FCSTD DOCUMENT  (FreeCAD 1.0R39285 (Git))
Label: GateValve
License: All rights reserved
LicenseURL: https://en.wikipedia.org/wiki/All_rights_reserved
objects: Part::Cylinder×23, Part::MultiFuse×20, Part::Cut×18, Part::Mirroring×12, Part::Box×12, Part::FeaturePython×11, Part::Feature×11, Sketcher::SketchObject×6, PartDesign::Pad×6, PartDesign::Body×6, Part::Torus×6, Part::MultiCommon×3
note: 152 computed .brp shape members not serialized (recipe doc carries the construction recipe); baked Part::Feature solids carry a one-line shape summary decoded from their .brp

FEATURE [Part::FeaturePython] Tube  label="IGP_Bellow"  # WARN: FeaturePython — macro-defined, semantics opaque (R4)
  AttacherType = Attacher::AttachEngine3D
  Height = 47
  InnerRadius = 11
  OuterRadius = 12.5
  Placement = pos=(0,0,114) rot=(0,1,0;0rad)
FEATURE [Part::Feature] Part__Feature1456  label="PrecursorTMP"
  Placement = pos=(0,40,0) rot=(0,1,0;1.5708rad)
  shape: bbox 254 x 24.64 x 254 mm, 51 faces (baked)
FEATURE [Part::Feature] Part__Feature  label="wh"
  Placement = pos=(0,0,0) rot=(1,0,0;1.5708rad)
  shape: bbox 69.9 x 69.9 x 12.7 mm, 278 faces (baked)
FEATURE [Part::FeaturePython] Tube001  # WARN: FeaturePython — macro-defined, semantics opaque (R4)
  AttacherType = Attacher::AttachEngine3D
  Height = 10.5
  InnerRadius = 32
  OuterRadius = 34.95
  Placement = pos=(0,0,1) rot=(0,0,1;0rad)
FEATURE [Part::MultiFuse] Fusion001  label="PreIGP"
  Placement = pos=(0,20,0) rot=(1,0,0;4.71239rad)
  Shapes = -> [Part__Feature,Tube001]
FEATURE [Part::Feature] Part__Feature1457  label="190094"
  shape: bbox 152.3 x 19.8 x 152.3 mm, 298 faces (baked)
FEATURE [Part::FeaturePython] Tube002  # WARN: FeaturePython — macro-defined, semantics opaque (R4)
  AttacherType = Attacher::AttachEngine3D
  Height = 18
  InnerRadius = 74
  OuterRadius = 76.15
  Placement = pos=(0,19,0) rot=(1,0,0;1.5708rad)
FEATURE [Part::MultiFuse] Fusion002  label="BAFlange"
  Placement = pos=(0,25,0) rot=(0,0,1;0rad)
  Shapes = -> [Part__Feature1457,Tube002]
FEATURE [Part::FeaturePython] Tube003  # WARN: FeaturePython — macro-defined, semantics opaque (R4)
  AttacherType = Attacher::AttachEngine3D
  Height = 20
  InnerRadius = 100
  OuterRadius = 110
  Placement = pos=(0,40,0) rot=(1,0,0;1.5708rad)
FEATURE [Part::MultiFuse] Fusion
  Shapes = -> [Part__Feature1456,Tube003]
FEATURE [Part::Mirroring] Part__Mirroring  label="PrecTMP"
  Base = (0,0,0)
  Normal = (0,1,0)
  Source = -> Fusion
FEATURE [Part::Box] Box  label="Cube"
  AttacherType = Attacher::AttachEngine3D
  Height = 500
  Length = 240
  Placement = pos=(-120,-25,-150) rot=(0,0,1;0rad)
  Width = 50
FEATURE [Part::FeaturePython] Tube004  # WARN: FeaturePython — macro-defined, semantics opaque (R4)
  AttacherType = Attacher::AttachEngine3D
  Height = 100
  InnerRadius = 0
  OuterRadius = 100
  Placement = pos=(0,40,0) rot=(1,0,0;1.5708rad)
FEATURE [Part::Cut] Cut
  Base = -> Box
  Tool = -> Tube004
FEATURE [Part::FeaturePython] Tube005  # WARN: FeaturePython — macro-defined, semantics opaque (R4)
  AttacherType = Attacher::AttachEngine3D
  Height = 12
  InnerRadius = 52
  OuterRadius = 58
  Placement = pos=(0,25,0) rot=(1,0,0;1.5708rad)
FEATURE [Part::MultiFuse] Fusion004
  Shapes = -> [Tube005,Fusion002]
FEATURE [Part::Mirroring] Part__Mirroring001  label="Gague"
  Base = (0,0,0)
  Normal = (0,1,0)
  Source = -> Fusion004
FEATURE [Part::Box] Box002  label="Cube002"
  AttacherType = Attacher::AttachEngine3D
  Height = 300
  Length = 140
  Placement = pos=(-70,-17,-90) rot=(0,0,1;0rad)
  Width = 34
FEATURE [Part::FeaturePython] Tube006  # WARN: FeaturePython — macro-defined, semantics opaque (R4)
  AttacherType = Attacher::AttachEngine3D
  Height = 100
  InnerRadius = 0
  OuterRadius = 52
  Placement = pos=(0,50,0) rot=(1,0,0;1.5708rad)
FEATURE [Part::Cut] Cut002
  Base = -> Box002
  Tool = -> Tube006
FEATURE [Part::FeaturePython] Tube007  # WARN: FeaturePython — macro-defined, semantics opaque (R4)
  AttacherType = Attacher::AttachEngine3D
  Height = 8
  InnerRadius = 20
  OuterRadius = 25
  Placement = pos=(0,20,0) rot=(1,0,0;1.5708rad)
FEATURE [Part::MultiFuse] Fusion006
  Shapes = -> [Tube007,Fusion001]
FEATURE [Part::Mirroring] Part__Mirroring002  label="Flangelets"
  Base = (0,0,0)
  Normal = (0,1,0)
  Source = -> Fusion006
FEATURE [Part::Box] Box004  label="Cube004"
  AttacherType = Attacher::AttachEngine3D
  Height = 168
  Length = 60
  Placement = pos=(-30,-14,-58) rot=(0,0,1;0rad)
  Width = 28
FEATURE [Part::FeaturePython] Tube008  # WARN: FeaturePython — macro-defined, semantics opaque (R4)
  AttacherType = Attacher::AttachEngine3D
  Height = 100
  InnerRadius = 0
  OuterRadius = 20
  Placement = pos=(0,50,0) rot=(1,0,0;1.5708rad)
FEATURE [Sketcher::SketchObject] Sketch
  ArcFitTolerance = 1e-06
  AttachmentSupport = -> [YZ_Plane]
  FullyConstrained = true
  MakeInternals = false
  MapMode = 5
  Placement = pos=(0,0,0) rot=(0.57735,0.57735,0.57735;2.0944rad)
  sketch-geometry (4):
    g0: LineSegment StartX=0 StartY=0 StartZ=0 EndX=10 EndY=0 EndZ=0
    g1: LineSegment StartX=0 StartY=0 StartZ=0 EndX=0 EndY=-156 EndZ=0
    g2: LineSegment StartX=0 StartY=-156 StartZ=0 EndX=4 EndY=-156 EndZ=0
    g3: LineSegment StartX=10 StartY=0 StartZ=0 EndX=4 EndY=-156 EndZ=0
  constraints (11):
    c: Distance(g0) = 10
    c: Coincident(g0,g-1)
    c: PointOnObject(g0,g-1)
    c: Distance(g1) = 156
    c: Coincident(g1,g0)
    c: Vertical(g1)
    c: Distance(g2) = 4
    c: Coincident(g2,g1)
    c: Horizontal(g2)
    c: Coincident(g3,g0)
    c: Coincident(g3,g2)
FEATURE [PartDesign::Pad] Pad
  Direction = (1,0,0)
  Length = 52
  Length2 = 10
  Placement = pos=(0,0,0) rot=(1,1,1;2.0944rad)
  Profile = -> Sketch
  ReferenceAxis = -> Sketch [N_Axis]
  Refine = true
  Suppressed = false
  Type = 0
FEATURE [PartDesign::Body] Body
  AllowCompound = false
  Group = -> [Sketch,Pad]
  Origin = -> Origin
  Placement = pos=(0,0,110) rot=(0,0,1;0rad)
  Tip = -> Pad
FEATURE [Part::Mirroring] Part__Mirroring003  label="Body (Mirror #4)"
  Base = (0,0,0)
  Normal = (0,1,0)
  Source = -> Body
FEATURE [Part::MultiFuse] Fusion008
  Placement = pos=(-26,0,0) rot=(0,0,1;0rad)
  Shapes = -> [Part__Mirroring003,Body]
FEATURE [Part::Cut] Cut004
  Base = -> Box004
  Tool = -> Fusion008
FEATURE [Part::Cut] Cut005
  Base = -> Cut004
  Tool = -> Tube008
FEATURE [Part::MultiFuse] Fusion009  label="eeijre"
  Shapes = -> [Part__Mirroring002,Fusion006,Cut005]
FEATURE [Sketcher::SketchObject] Sketch001
  ArcFitTolerance = 1e-06
  AttachmentSupport = -> [YZ_Plane001]
  FullyConstrained = false
  MakeInternals = false
  MapMode = 5
  Placement = pos=(0,0,0) rot=(0.57735,0.57735,0.57735;2.0944rad)
  sketch-geometry (4):
    g0: LineSegment StartX=0 StartY=0 StartZ=0 EndX=12 EndY=0 EndZ=0
    g1: LineSegment StartX=0 StartY=0 StartZ=0 EndX=0 EndY=-294 EndZ=0
    g2: LineSegment StartX=0 StartY=-294 StartZ=0 EndX=5 EndY=-294 EndZ=0
    g3: LineSegment StartX=12 StartY=0 StartZ=0 EndX=5 EndY=-294 EndZ=0
  constraints (9):
    c: Distance(g0) = 12
    c: Coincident(g0,g-1)
    c: PointOnObject(g0,g-1)
    c: Distance(g1) = 294
    c: Coincident(g1,g0)
    c: Vertical(g1)
    c: Distance(g2) = 5
    c: Coincident(g2,g1)
    c: Horizontal(g2)
FEATURE [PartDesign::Pad] Pad001
  Direction = (1,0,0)
  Length = 128
  Length2 = 10
  Placement = pos=(0,0,0) rot=(1,1,1;2.0944rad)
  Profile = -> Sketch001
  ReferenceAxis = -> Sketch001 [N_Axis]
  Refine = true
  Suppressed = false
  Type = 0
FEATURE [PartDesign::Body] Body001
  AllowCompound = false
  Group = -> [Sketch001,Pad001]
  Origin = -> Origin001
  Placement = pos=(0,0,210) rot=(0,0,1;0rad)
  Tip = -> Pad001
FEATURE [Part::Mirroring] Part__Mirroring004  label="Body001 (Mirror #5)"
  Base = (0,0,0)
  Normal = (0,1,0)
  Source = -> Body001
FEATURE [Part::MultiFuse] Fusion010
  Placement = pos=(-64,0,0) rot=(0,0,1;0rad)
  Shapes = -> [Part__Mirroring004,Body001]
FEATURE [Part::Cut] Cut006
  Base = -> Cut002
  Tool = -> Fusion010
FEATURE [Part::MultiFuse] Fusion011  label="sds"
  Shapes = -> [Fusion004,Part__Mirroring001,Cut006]
FEATURE [Sketcher::SketchObject] Sketch002
  ArcFitTolerance = 1e-06
  AttachmentSupport = -> [YZ_Plane002]
  FullyConstrained = false
  MakeInternals = false
  MapMode = 5
  Placement = pos=(0,0,0) rot=(0.57735,0.57735,0.57735;2.0944rad)
  sketch-geometry (4):
    g0: LineSegment StartX=0 StartY=0 StartZ=0 EndX=0 EndY=-490 EndZ=0
    g1: LineSegment StartX=0 StartY=0 StartZ=0 EndX=15 EndY=0 EndZ=0
    g2: LineSegment StartX=0 StartY=-490 StartZ=0 EndX=5 EndY=-490 EndZ=0
    g3: LineSegment StartX=15 StartY=0 StartZ=0 EndX=5 EndY=-490 EndZ=0
  constraints (9):
    c: Distance(g0) = 490
    c: Coincident(g0,g-1)
    c: Vertical(g0)
    c: Distance(g1) = 15
    c: Coincident(g1,g0)
    c: PointOnObject(g1,g-1)
    c: Distance(g2) = 5
    c: Coincident(g2,g0)
    c: Horizontal(g2)
FEATURE [PartDesign::Pad] Pad002
  Direction = (1,0,0)
  Length = 220
  Length2 = 10
  Placement = pos=(0,0,0) rot=(1,1,1;2.0944rad)
  Profile = -> Sketch002
  ReferenceAxis = -> Sketch002 [N_Axis]
  Refine = true
  Suppressed = false
  Type = 0
FEATURE [PartDesign::Body] Body002
  AllowCompound = false
  Group = -> [Sketch002,Pad002]
  Origin = -> Origin002
  Tip = -> Pad002
FEATURE [Part::Mirroring] Part__Mirroring005  label="Body002 (Mirror #6)"
  Base = (0,0,0)
  Normal = (0,1,0)
  Source = -> Body002
FEATURE [Part::MultiFuse] Fusion012
  Placement = pos=(-110,0,350) rot=(0,0,1;0rad)
  Shapes = -> [Part__Mirroring005,Body002]
FEATURE [Part::Cut] Cut007
  Base = -> Cut
  Tool = -> Fusion012
FEATURE [Part::MultiFuse] Fusion013  label="sxj"
  Shapes = -> [Part__Mirroring,Fusion,Cut007]
FEATURE [Part::Cylinder] Cylinder
  Angle = 360
  AttacherType = Attacher::AttachEngine3D
  FirstAngle = 0
  Height = 30
  Placement = pos=(0,15,0) rot=(1,0,0;1.5708rad)
  Radius = 108
  SecondAngle = 0
FEATURE [Sketcher::SketchObject] Sketch003
  ArcFitTolerance = 1e-06
  AttachmentSupport = -> [YZ_Plane003]
  FullyConstrained = false
  MakeInternals = false
  MapMode = 5
  Placement = pos=(0,0,0) rot=(0.57735,0.57735,0.57735;2.0944rad)
  sketch-geometry (4):
    g0: LineSegment StartX=0 StartY=0 StartZ=0 EndX=0 EndY=-490 EndZ=0
    g1: LineSegment StartX=0 StartY=0 StartZ=0 EndX=15 EndY=0 EndZ=0
    g2: LineSegment StartX=0 StartY=-490 StartZ=0 EndX=5 EndY=-490 EndZ=0
    g3: LineSegment StartX=15 StartY=0 StartZ=0 EndX=5 EndY=-490 EndZ=0
  constraints (9):
    c: Distance(g0) = 490
    c: Coincident(g0,g-1)
    c: Vertical(g0)
    c: Distance(g1) = 15
    c: Coincident(g1,g0)
    c: PointOnObject(g1,g-1)
    c: Distance(g2) = 5
    c: Coincident(g2,g0)
    c: Horizontal(g2)
FEATURE [PartDesign::Pad] Pad003
  Direction = (1,0,0)
  Length = 220
  Length2 = 10
  Placement = pos=(0,0,0) rot=(1,1,1;2.0944rad)
  Profile = -> Sketch003
  ReferenceAxis = -> Sketch003 [N_Axis]
  Refine = true
  Suppressed = false
  Type = 0
FEATURE [PartDesign::Body] Body003
  AllowCompound = false
  Group = -> [Sketch003,Pad003]
  Origin = -> Origin003
  Tip = -> Pad003
FEATURE [Part::Mirroring] Part__Mirroring006  label="Body002 (Mirror #6)001"
  Base = (0,0,0)
  Normal = (0,1,0)
  Source = -> Body003
FEATURE [Part::MultiFuse] Fusion014
  Placement = pos=(-110,0,350) rot=(0,0,1;0rad)
  Shapes = -> [Part__Mirroring006,Body003]
FEATURE [Part::MultiCommon] Common  label="Gate_TMP"
  Shapes = -> [Cylinder,Fusion014]
FEATURE [Part::Cylinder] Cylinder001
  Angle = 360
  AttacherType = Attacher::AttachEngine3D
  FirstAngle = 0
  Height = 24
  Placement = pos=(0,12,0) rot=(1,0,0;1.5708rad)
  Radius = 62
  SecondAngle = 0
FEATURE [Sketcher::SketchObject] Sketch004
  ArcFitTolerance = 1e-06
  AttachmentSupport = -> [YZ_Plane004]
  FullyConstrained = false
  MakeInternals = false
  MapMode = 5
  Placement = pos=(0,0,0) rot=(0.57735,0.57735,0.57735;2.0944rad)
  sketch-geometry (4):
    g0: LineSegment StartX=0 StartY=0 StartZ=0 EndX=12 EndY=0 EndZ=0
    g1: LineSegment StartX=0 StartY=0 StartZ=0 EndX=0 EndY=-294 EndZ=0
    g2: LineSegment StartX=0 StartY=-294 StartZ=0 EndX=5 EndY=-294 EndZ=0
    g3: LineSegment StartX=12 StartY=0 StartZ=0 EndX=5 EndY=-294 EndZ=0
  constraints (9):
    c: Distance(g0) = 12
    c: Coincident(g0,g-1)
    c: PointOnObject(g0,g-1)
    c: Distance(g1) = 294
    c: Coincident(g1,g0)
    c: Vertical(g1)
    c: Distance(g2) = 5
    c: Coincident(g2,g1)
    c: Horizontal(g2)
FEATURE [PartDesign::Pad] Pad004
  Direction = (1,0,0)
  Length = 128
  Length2 = 10
  Placement = pos=(0,0,0) rot=(1,1,1;2.0944rad)
  Profile = -> Sketch004
  ReferenceAxis = -> Sketch004 [N_Axis]
  Refine = true
  Suppressed = false
  Type = 0
FEATURE [PartDesign::Body] Body004
  AllowCompound = false
  Group = -> [Sketch004,Pad004]
  Origin = -> Origin004
  Placement = pos=(0,0,210) rot=(0,0,1;0rad)
  Tip = -> Pad004
FEATURE [Part::Mirroring] Part__Mirroring007  label="Body001 (Mirror #5)001"
  Base = (0,0,0)
  Normal = (0,1,0)
  Source = -> Body004
FEATURE [Part::MultiFuse] Fusion015
  Placement = pos=(-64,0,0) rot=(0,0,1;0rad)
  Shapes = -> [Part__Mirroring007,Body004]
FEATURE [Part::MultiCommon] Common001  label="Gate_BA"
  Shapes = -> [Fusion015,Cylinder001]
FEATURE [Part::Cylinder] Cylinder002
  Angle = 360
  AttacherType = Attacher::AttachEngine3D
  FirstAngle = 0
  Height = 20
  Placement = pos=(0,10,0) rot=(1,0,0;1.5708rad)
  Radius = 25
  SecondAngle = 0
FEATURE [Sketcher::SketchObject] Sketch005
  ArcFitTolerance = 1e-06
  AttachmentSupport = -> [YZ_Plane005]
  FullyConstrained = true
  MakeInternals = false
  MapMode = 5
  Placement = pos=(0,0,0) rot=(0.57735,0.57735,0.57735;2.0944rad)
  sketch-geometry (4):
    g0: LineSegment StartX=0 StartY=0 StartZ=0 EndX=10 EndY=0 EndZ=0
    g1: LineSegment StartX=0 StartY=0 StartZ=0 EndX=0 EndY=-156 EndZ=0
    g2: LineSegment StartX=0 StartY=-156 StartZ=0 EndX=4 EndY=-156 EndZ=0
    g3: LineSegment StartX=10 StartY=0 StartZ=0 EndX=4 EndY=-156 EndZ=0
  constraints (11):
    c: Distance(g0) = 10
    c: Coincident(g0,g-1)
    c: PointOnObject(g0,g-1)
    c: Distance(g1) = 156
    c: Coincident(g1,g0)
    c: Vertical(g1)
    c: Distance(g2) = 4
    c: Coincident(g2,g1)
    c: Horizontal(g2)
    c: Coincident(g3,g0)
    c: Coincident(g3,g2)
FEATURE [PartDesign::Pad] Pad005
  Direction = (1,0,0)
  Length = 52
  Length2 = 10
  Placement = pos=(0,0,0) rot=(1,1,1;2.0944rad)
  Profile = -> Sketch005
  ReferenceAxis = -> Sketch005 [N_Axis]
  Refine = true
  Suppressed = false
  Type = 0
FEATURE [PartDesign::Body] Body005
  AllowCompound = false
  Group = -> [Sketch005,Pad005]
  Origin = -> Origin005
  Placement = pos=(0,0,110) rot=(0,0,1;0rad)
  Tip = -> Pad005
FEATURE [Part::Mirroring] Part__Mirroring008  label="Body (Mirror #4)001"
  Base = (0,0,0)
  Normal = (0,1,0)
  Source = -> Body005
FEATURE [Part::MultiFuse] Fusion016
  Placement = pos=(-26,0,0) rot=(0,0,1;0rad)
  Shapes = -> [Part__Mirroring008,Body005]
FEATURE [Part::MultiCommon] Common002  label="sdjisj"
  Shapes = -> [Cylinder002,Fusion016]
FEATURE [Part::Feature] Part__Feature1458  label="M3_300mm"
  Placement = pos=(0,0,0) rot=(0,1,0;1.5708rad)
  shape: bbox 3.527 x 3.054 x 300.4 mm, 1334 faces (baked)
FEATURE [Part::Feature] Part__Feature1459  label="M3_300mm001"
  Placement = pos=(0,0,104) rot=(0,1,0;1.5708rad)
  shape: bbox 3.527 x 3.054 x 300.4 mm, 1334 faces (baked)
FEATURE [Part::Box] Box005  label="Cube005"
  AttacherType = Attacher::AttachEngine3D
  Height = 1000
  Length = 1000
  Placement = pos=(-500,-500,105) rot=(0,0,1;0rad)
  Width = 1000
FEATURE [Part::Cut] Cut008  label="sdss"
  Base = -> Part__Feature1459
  Tool = -> Box005
FEATURE [Part::Cylinder] Cylinder003
  Angle = 360
  AttacherType = Attacher::AttachEngine3D
  FirstAngle = 0
  Height = 8
  Placement = pos=(0,0,-54) rot=(0,0,1;0rad)
  Radius = 1.5
  SecondAngle = 0
FEATURE [Part::Cylinder] Cylinder004
  Angle = 360
  AttacherType = Attacher::AttachEngine3D
  FirstAngle = 0
  Height = 8
  Placement = pos=(0,0,-54) rot=(0,0,1;0rad)
  Radius = 1.75
  SecondAngle = 0
FEATURE [Part::Cut] Cut009  label="IGP"
  Base = -> Fusion009
  Tool = -> Cylinder004
FEATURE [Part::Cylinder] Cylinder005
  Angle = 360
  AttacherType = Attacher::AttachEngine3D
  FirstAngle = 0
  Height = 20
  Placement = pos=(0,0,105) rot=(0,0,1;0rad)
  Radius = 1.5
  SecondAngle = 0
FEATURE [Part::Cylinder] Cylinder006
  Angle = 360
  AttacherType = Attacher::AttachEngine3D
  FirstAngle = 0
  Height = 3
  Placement = pos=(0,0,115) rot=(0,0,1;0rad)
  Radius = 3
  SecondAngle = 0
FEATURE [Part::Torus] Torus
  Angle1 = -180
  Angle2 = 180
  Angle3 = 90
  AttacherType = Attacher::AttachEngine3D
  Placement = pos=(-3,0,125) rot=(1,0,0;1.5708rad)
  Radius1 = 3
  Radius2 = 1.5
FEATURE [Part::Torus] Torus001
  Angle1 = -180
  Angle2 = 180
  Angle3 = 90
  AttacherType = Attacher::AttachEngine3D
  Placement = pos=(0,0,0) rot=(1,0,0;4.71239rad)
  Radius1 = 3
  Radius2 = 1.5
FEATURE [Part::Mirroring] Part__Mirroring009  label="Torus001 (Mirror #10)"
  Base = (0,0,0)
  Normal = (1,0,0)
  Placement = pos=(-3,0,131) rot=(0,0,1;0rad)
  Source = -> Torus001
FEATURE [Part::Cylinder] Cylinder008
  Angle = 360
  AttacherType = Attacher::AttachEngine3D
  FirstAngle = 0
  Height = 30
  Placement = pos=(-6,0,131) rot=(0,0,1;0rad)
  Radius = 1.5
  SecondAngle = 0
FEATURE [Part::MultiFuse] Fusion017  label="IGP_Thread"
  Shapes = -> [Part__Mirroring009,Cylinder008,Torus,Cylinder006,Cylinder005,Cylinder003,Cut008]
FEATURE [Part::Box] Box006  label="Cube006"
  AttacherType = Attacher::AttachEngine3D
  Height = 4
  Length = 60
  Placement = pos=(-30,-14,110) rot=(0,0,1;0rad)
  Width = 28
FEATURE [Part::Cylinder] Cylinder009
  Angle = 360
  AttacherType = Attacher::AttachEngine3D
  FirstAngle = 0
  Height = 20
  Placement = pos=(0,0,105) rot=(0,0,1;0rad)
  Radius = 1.75
  SecondAngle = 0
FEATURE [Part::Cut] Cut010  label="IGP_Cap"
  Base = -> Box006
  Tool = -> Cylinder009
FEATURE [Part::Cylinder] Cylinder010  label="IGP_Bellow_Cap"
  Angle = 360
  AttacherType = Attacher::AttachEngine3D
  FirstAngle = 0
  Height = 4
  Placement = pos=(0,0,161) rot=(0,0,1;0rad)
  Radius = 12.5
  SecondAngle = 0
FEATURE [Part::Box] Box007  label="Cube007"
  AttacherType = Attacher::AttachEngine3D
  Height = 1000
  Length = 1000
  Placement = pos=(-500,-500,105) rot=(0,0,1;0rad)
  Width = 1000
FEATURE [Part::Feature] Part__Feature1460  label="M3_300mm002"
  Placement = pos=(0,0,104) rot=(0,1,0;1.5708rad)
  shape: bbox 3.527 x 3.054 x 300.4 mm, 1334 faces (baked)
FEATURE [Part::Cut] Cut011  label="sdss001"
  Base = -> Part__Feature1460
  Tool = -> Box007
FEATURE [Part::Cut] Cut012  label="IGP_Gate"
  Base = -> Common002
  Tool = -> Cut011
FEATURE [Part::Feature] Part__Feature1461  label="M5_300mm"
  Placement = pos=(0,0,10) rot=(0,1,0;1.5708rad)
  shape: bbox 5.087 x 5.087 x 300.7 mm, 836 faces (baked)
FEATURE [Part::Feature] Part__Feature1462  label="M5_300mm001"
  Placement = pos=(0,0,310) rot=(0,1,0;1.5708rad)
  shape: bbox 5.087 x 5.087 x 300.7 mm, 836 faces (baked)
FEATURE [Part::Box] Box008  label="Cube008"
  AttacherType = Attacher::AttachEngine3D
  Height = 200
  Length = 10
  Placement = pos=(-5,-5,340) rot=(0,0,1;0rad)
  Width = 10
FEATURE [Part::Cut] Cut013
  Base = -> Part__Feature1462
  Tool = -> Box008
FEATURE [Part::Feature] Part__Feature1463  label="M5_300mm002"
  Placement = pos=(0,0,10) rot=(0,1,0;1.5708rad)
  shape: bbox 5.087 x 5.087 x 300.7 mm, 836 faces (baked)
FEATURE [Part::MultiFuse] Fusion018  label="TurboThread"
  Shapes = -> [Cut013,Part__Feature1463]
FEATURE [Part::Cylinder] Cylinder011
  Angle = 360
  AttacherType = Attacher::AttachEngine3D
  FirstAngle = 0
  Height = 15
  Placement = pos=(0,0,-155) rot=(0,0,1;0rad)
  Radius = 2.5
  SecondAngle = 0
FEATURE [Part::Cylinder] Cylinder012
  Angle = 360
  AttacherType = Attacher::AttachEngine3D
  FirstAngle = 0
  Height = 15
  Placement = pos=(0,0,-155) rot=(0,0,1;0rad)
  Radius = 2.75
  SecondAngle = 0
FEATURE [Part::Cylinder] Cylinder013
  Angle = 360
  AttacherType = Attacher::AttachEngine3D
  FirstAngle = 0
  Height = 35
  Placement = pos=(-10,0,395) rot=(0,0,1;0rad)
  Radius = 2.5
  SecondAngle = 0
FEATURE [Part::Cylinder] Cylinder014
  Angle = 360
  AttacherType = Attacher::AttachEngine3D
  FirstAngle = 0
  Height = 10
  Placement = pos=(0,0,360) rot=(0,0,1;0rad)
  Radius = 5
  SecondAngle = 0
FEATURE [Part::Box] Box009  label="Cube009"
  AttacherType = Attacher::AttachEngine3D
  Height = 10
  Length = 240
  Placement = pos=(-120,-25,350) rot=(0,0,1;0rad)
  Width = 50
FEATURE [Part::Cylinder] Cylinder015
  Angle = 360
  AttacherType = Attacher::AttachEngine3D
  FirstAngle = 0
  Height = 35
  Placement = pos=(0,0,340) rot=(0,0,1;0rad)
  Radius = 2.75
  SecondAngle = 0
FEATURE [Part::Cut] Cut015  label="TMP_Cap"
  Base = -> Box009
  Tool = -> Cylinder015
FEATURE [Part::Torus] Torus002
  Angle1 = -180
  Angle2 = 180
  Angle3 = 90
  AttacherType = Attacher::AttachEngine3D
  Placement = pos=(-5,0,385) rot=(1,0,0;1.5708rad)
  Radius1 = 5
  Radius2 = 2.5
FEATURE [Part::Torus] Torus003
  Angle1 = -180
  Angle2 = 180
  Angle3 = 90
  AttacherType = Attacher::AttachEngine3D
  Placement = pos=(0,0,0) rot=(1,0,0;4.71239rad)
  Radius1 = 5
  Radius2 = 2.5
FEATURE [Part::Mirroring] Part__Mirroring010  label="Torus003 (Mirror #11)"
  Base = (0,0,0)
  Normal = (1,0,0)
  Placement = pos=(-5,0,395) rot=(0,0,1;0rad)
  Source = -> Torus003
FEATURE [Part::Cylinder] Cylinder017
  Angle = 360
  AttacherType = Attacher::AttachEngine3D
  FirstAngle = 0
  Height = 45
  Placement = pos=(0,0,340) rot=(0,0,1;0rad)
  Radius = 2.5
  SecondAngle = 0
FEATURE [Part::FeaturePython] Tube009  label="TMP_Bellow"  # WARN: FeaturePython — macro-defined, semantics opaque (R4)
  AttacherType = Attacher::AttachEngine3D
  Height = 80
  InnerRadius = 11
  OuterRadius = 12.5
  Placement = pos=(-3,0,350) rot=(0,1,0;0rad)
FEATURE [Part::Cylinder] Cylinder018  label="TMP_Bellow_Cap"
  Angle = 360
  AttacherType = Attacher::AttachEngine3D
  FirstAngle = 0
  Height = 4
  Placement = pos=(-3,0,430) rot=(0,0,1;0rad)
  Radius = 12.5
  SecondAngle = 0
FEATURE [Part::Feature] Part__Feature1464  label="M5_300mm003"
  Placement = pos=(0,0,10) rot=(0,1,0;1.5708rad)
  shape: bbox 5.087 x 5.087 x 300.7 mm, 836 faces (baked)
FEATURE [Part::Cut] Cut016  label="TMP_Gate"
  Base = -> Common
  Tool = -> Part__Feature1464
FEATURE [Part::Feature] Part__Feature1466  label="M3_300mm004"
  Placement = pos=(0,0,66) rot=(0,1,0;1.5708rad)
  shape: bbox 3.527 x 3.054 x 300.4 mm, 1334 faces (baked)
FEATURE [Part::MultiFuse] Fusion019  label="TMP_Thread"
  Shapes = -> [Cylinder017,Part__Mirroring010,Torus002,Cylinder014,Cylinder013,Cylinder011,Fusion018]
FEATURE [Part::Box] Box010  label="Cube010"
  AttacherType = Attacher::AttachEngine3D
  Height = 10
  Length = 240
  Placement = pos=(-120,-25,-160) rot=(0,0,1;0rad)
  Width = 50
FEATURE [Part::MultiFuse] Fusion020
  Shapes = -> [Fusion013,Box010]
FEATURE [Part::Cut] Cut017  label="TMP"
  Base = -> Fusion020
  Tool = -> Cylinder012
FEATURE [Part::Box] Box011  label="Cube011"
  AttacherType = Attacher::AttachEngine3D
  Height = 30
  Length = 10
  Placement = pos=(-5,-5,200) rot=(0,0,1;0rad)
  Width = 10
FEATURE [Part::Cut] Cut018
  Base = -> Part__Feature1466
  Tool = -> Box011
FEATURE [Part::Box] Box012  label="Cube012"
  AttacherType = Attacher::AttachEngine3D
  Height = 10
  Length = 140
  Placement = pos=(-70,-17,-100) rot=(0,0,1;0rad)
  Width = 34
FEATURE [Part::MultiFuse] Fusion021
  Shapes = -> [Fusion011,Box012]
FEATURE [Part::Cylinder] Cylinder019
  Angle = 360
  AttacherType = Attacher::AttachEngine3D
  FirstAngle = 0
  Height = 10
  Placement = pos=(0,0,-94) rot=(0,0,1;0rad)
  Radius = 1.75
  SecondAngle = 0
FEATURE [Part::Cut] Cut019  label="BA"
  Base = -> Fusion021
  Tool = -> Cylinder019
FEATURE [Part::Cylinder] Cylinder020
  Angle = 360
  AttacherType = Attacher::AttachEngine3D
  FirstAngle = 0
  Height = 25
  Placement = pos=(0,0,200) rot=(0,0,1;0rad)
  Radius = 1.5
  SecondAngle = 0
FEATURE [Part::Box] Box013  label="Cube013"
  AttacherType = Attacher::AttachEngine3D
  Height = 6
  Length = 140
  Placement = pos=(-70,-17,210) rot=(0,0,1;0rad)
  Width = 34
FEATURE [Part::Cylinder] Cylinder021
  Angle = 360
  AttacherType = Attacher::AttachEngine3D
  FirstAngle = 0
  Height = 30
  Placement = pos=(0,0,200) rot=(0,0,1;0rad)
  Radius = 2
  SecondAngle = 0
FEATURE [Part::Cut] Cut020  label="BA_Cap"
  Base = -> Box013
  Tool = -> Cylinder021
FEATURE [Part::Cylinder] Cylinder022
  Angle = 360
  AttacherType = Attacher::AttachEngine3D
  FirstAngle = 0
  Height = 5
  Placement = pos=(0,0,216) rot=(0,0,1;0rad)
  Radius = 3
  SecondAngle = 0
FEATURE [Part::Torus] Torus004
  Angle1 = -180
  Angle2 = 180
  Angle3 = 90
  AttacherType = Attacher::AttachEngine3D
  Placement = pos=(-3,0,225) rot=(1,0,0;1.5708rad)
  Radius1 = 3
  Radius2 = 1.5
FEATURE [Part::Torus] Torus005
  Angle1 = -180
  Angle2 = 180
  Angle3 = 90
  AttacherType = Attacher::AttachEngine3D
  Placement = pos=(0,0,0) rot=(1,0,0;4.71239rad)
  Radius1 = 3
  Radius2 = 1.5
FEATURE [Part::Mirroring] Part__Mirroring011  label="Torus001 (Mirror #10)001"
  Base = (0,0,0)
  Normal = (1,0,0)
  Placement = pos=(-3,0,231) rot=(0,0,1;0rad)
  Source = -> Torus005
FEATURE [Part::Cylinder] Cylinder023
  Angle = 360
  AttacherType = Attacher::AttachEngine3D
  FirstAngle = 0
  Height = 32
  Placement = pos=(-6,0,231) rot=(0,0,1;0rad)
  Radius = 1.5
  SecondAngle = 0
FEATURE [Part::FeaturePython] Tube010  label="BA_Bellow"  # WARN: FeaturePython — macro-defined, semantics opaque (R4)
  AttacherType = Attacher::AttachEngine3D
  Height = 47
  InnerRadius = 11
  OuterRadius = 12.5
  Placement = pos=(0,0,216) rot=(0,1,0;0rad)
FEATURE [Part::MultiFuse] Fusion022  label="BA_Thread"
  Shapes = -> [Cylinder023,Part__Mirroring011,Torus004,Cylinder022,Cylinder020,Cut018]
FEATURE [Part::Cylinder] Cylinder024  label="BA_Bellow_Cap"
  Angle = 360
  AttacherType = Attacher::AttachEngine3D
  FirstAngle = 0
  Height = 4
  Placement = pos=(0,0,263) rot=(0,0,1;0rad)
  Radius = 12.5
  SecondAngle = 0
